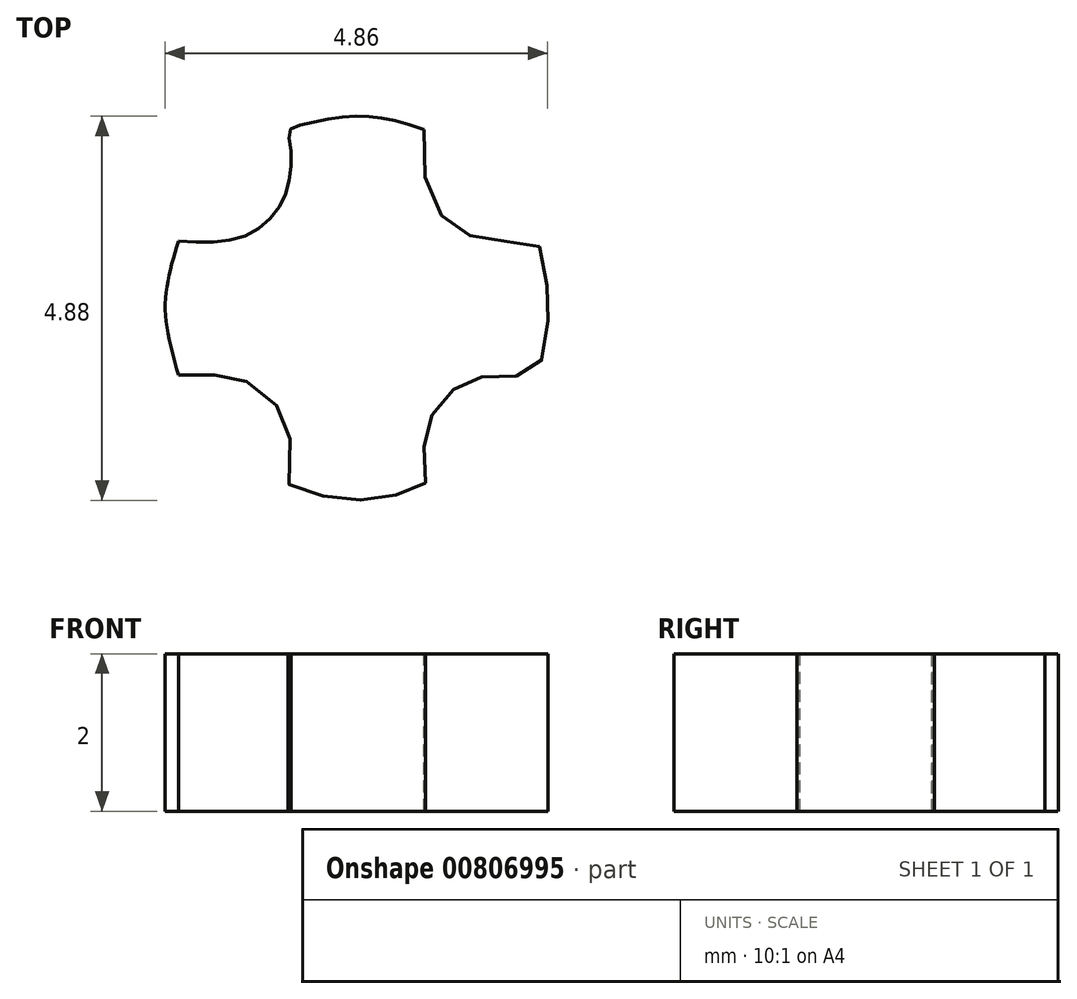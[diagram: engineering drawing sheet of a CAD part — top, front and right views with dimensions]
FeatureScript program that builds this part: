
annotation { "Feature Type Name" : "Feature", "Feature Type Description" : "" }
export const myFeature = defineFeature(function(context is Context, id is Id, definition is map)
    precondition{}
    {
        {
            var Q0;
            Q0=qCreatedBy(makeId("Top.planeOp"),FACE);
            var sketch = newSketch(context, id + "F0", { "sketchPlane" : qUnion([Q0])});
            skFitSpline(sketch, "E0", {"points": [v(-1.42, 1.42) * mm, v(-1.59, 2.3) * mm, v(-1.42, 3.12) * mm], "startDerivative": vector(-0.5, 1.75) * mm, "endDerivative": vector(0.5, 1.65) * mm});
            skFitSpline(sketch, "E1", {"points": [v(-1.42, 3.12) * mm, v(-0.86, 3.12) * mm, v(-0.42, 3.27) * mm, v(-0.12, 3.58) * mm, v(0, 3.93) * mm, v(0, 4.34) * mm, v(0, 4.54) * mm, v(0.24, 4.62) * mm, v(0.63, 4.7) * mm, v(0.97, 4.7) * mm, v(1.29, 4.66) * mm, v(1.7, 4.54) * mm], "startDerivative": vector(5.18, -0.26) * mm, "endDerivative": vector(4.37, -1.41) * mm});
            skFitSpline(sketch, "E2", {"points": [v(-1.42, 1.42) * mm, v(-1.13, 1.42) * mm, v(-0.88, 1.42) * mm, v(-0.69, 1.4) * mm, v(-0.35, 1.22) * mm, v(-0.16, 1.02) * mm, v(-0.04, 0.76) * mm, v(0, 0.44) * mm, v(0, 0) * mm, v(0.28, -0.09) * mm, v(0.57, -0.15) * mm, v(0.9, -0.17) * mm, v(1.18, -0.14) * mm, v(1.45, -0.08) * mm, v(1.7, 0) * mm, v(1.7, 0.2) * mm, v(1.7, 0.5) * mm, v(1.74, 0.76) * mm, v(1.82, 0.95) * mm, v(2, 1.17) * mm, v(2.13, 1.28) * mm, v(2.3, 1.37) * mm, v(2.56, 1.42) * mm, v(2.8, 1.42) * mm, v(3.12, 1.42) * mm, v(3.2, 1.68) * mm, v(3.26, 2.03) * mm, v(3.27, 2.3) * mm, v(3.26, 2.57) * mm, v(3.18, 2.94) * mm, v(3.12, 3.12) * mm, v(2.8, 3.12) * mm, v(2.53, 3.13) * mm, v(2.2, 3.23) * mm, v(2, 3.36) * mm, v(1.8, 3.63) * mm, v(1.7, 4.05) * mm, v(1.7, 4.54) * mm], "startDerivative": vector(10.87, -0.02) * mm, "endDerivative": vector(0.52, 14.17) * mm});
            skSolve(sketch);
        }
        {
            var Q0;
            Q0=makeQuery(id+"F0.imprint","IMPRINT",FACE,{"disambiguationData":[TD([[makeQuery(id+"F0.imprint","IMPRINT",EDGE,{"derivedFrom":sQuery(id+"F0.wireOp",EDGE,"E0")}),-1.0]])]});
            extrude(context, id + "F1", {"entities" : qUnion([Q0]), "depth" : 2 * mm, "offsetDistance" : 25 * mm});
        }
    });
